# Revit family: 94_MLRB32BAR + TLE31SS1J + M356W + MX60013 + AB612E
name_source: partatom
category: 衛生器具
units: mm (PartAtom-declared; Revit-internal decimal feet)

## family parameters
OmniClass タイトル = Sanitary, Laundry, and Cleaning Equipment
OmniClass 番号 = 23.45.00.00
パーツ タイプ = 標準
ロード時にボイドで切り取り = はい
丸型コネクタ寸法 = 直径を使用
作業面ベース = いいえ
共有 = いいえ
常に垂直 = はい
部屋計算ポイント = いいえ

## types (2) — shared parameters
3Dファイル形式 = rfa
BLCJ仕様バージョン = Version1.0
URL = https://jp.toto.com
キーノート = 0表示の場合は商品仕様と設計数量をご確認ください
データ作成ソフトVer = Revit ver.2019
パネル色 = TOTO_#NB12 コンフォウォームホワイト
モデル = MLRB32BAR + TLE31SS1J + M356W + MX60013 + AB612E
付属単位 = TLE31SS1J + M356W + MX60013 + AB612E
企業コード = 504860
使用水 = 上水
商品情報URL = https://www.com-et.com
商品紹介URL = https://jp.toto.com
奥行 = 325
幅 = 700
排水接続口 = 32
排水配管 = はい
構成品番 = MLRB32BAR + TLE31SS1J + M356W + MX60013 + AB612E
水配管 = はい
給水接続口 = 15
給水接続口情報 = R1/2
製品リリース年月 = 2022年08月
製品出荷対象 = 国内
製造元 = TOTO株式会社
説明 = カウンター一体形コーナー洗面器_間口700mm_奥行325mm_エプロンRタイプ
負荷分類 = 9_コンセント
陶器色 = <カテゴリ別>
zero-valued in all types: 上水負荷単位, 給湯負荷単位

## per-type parameters (varying)
| type | あふれ面高さ | カウンター色 | 周波数 | 排気配管 | 最低使用圧力 | 最高使用圧力 | 極数 | 消費電力 | 温水配管 | 相 | 電圧 |
| あふれ面高さ(750mm) | 750  [stored 2.46063 ft] | TOTO_陶器・便座♯NW1 | 0 | はい | 0.1 MPa | 0.8 MPa | 2 | 20W | はい | 1 | 100V |
| あふれ面高さ(800mm) | 800  [stored 2.62467 ft] | TOTO_#PA13 パルフェクールホワイト |  | いいえ | 0.0 MPa | 0.0 MPa |  |  | いいえ |  |  |

note: [stored X ft] marks values corroborated as IEEE doubles in the binary element streams (Revit-internal decimal feet)
